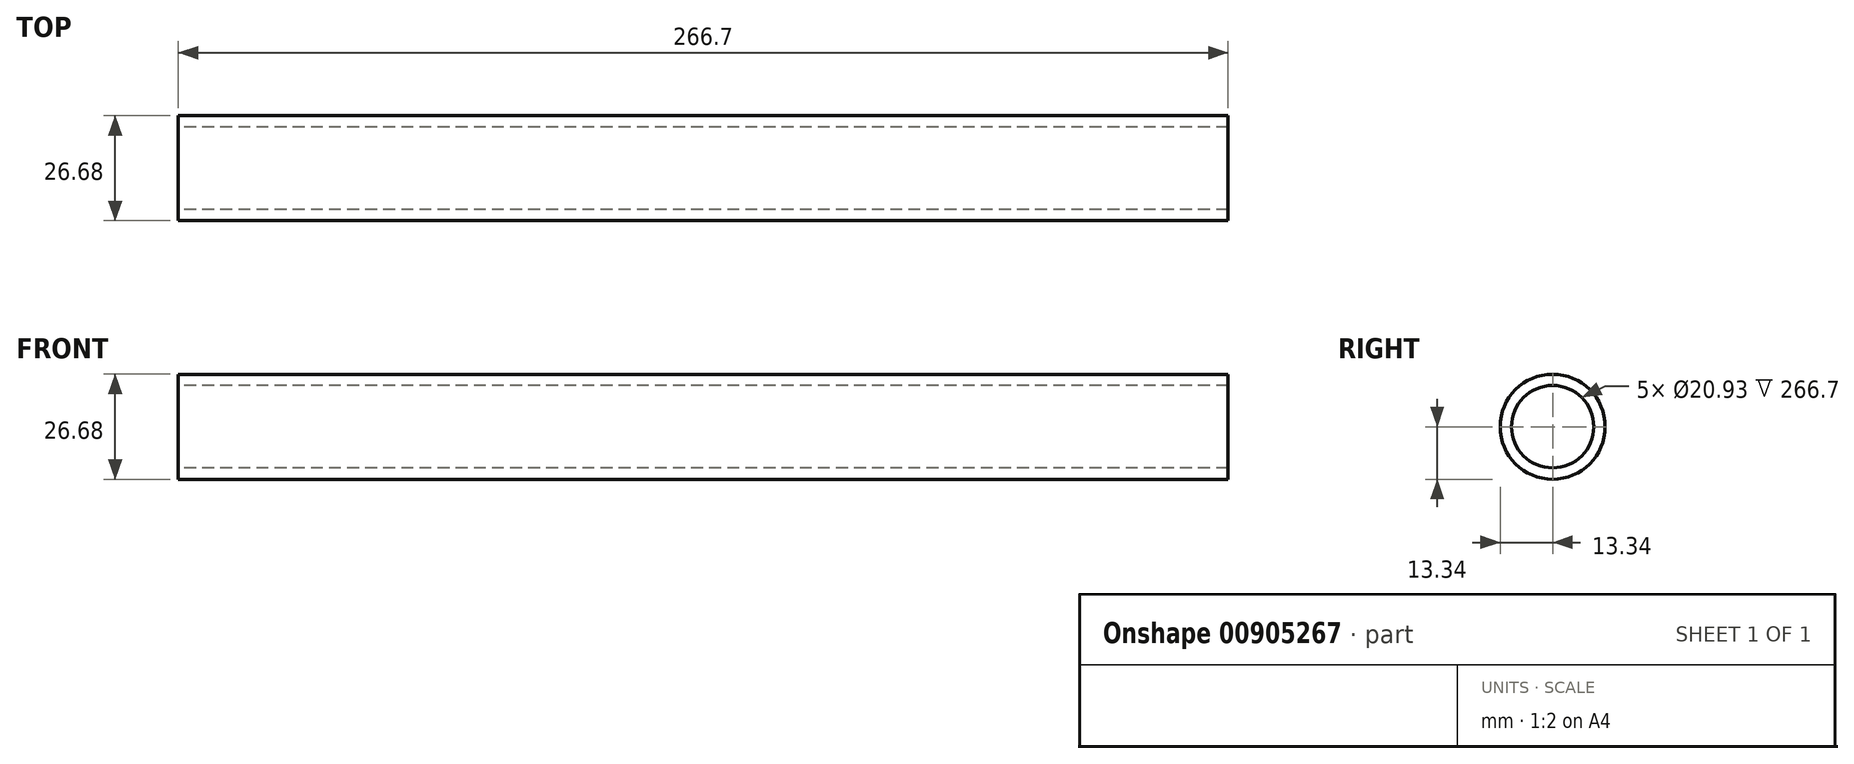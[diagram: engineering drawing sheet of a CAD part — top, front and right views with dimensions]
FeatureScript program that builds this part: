
annotation { "Feature Type Name" : "Feature", "Feature Type Description" : "" }
export const myFeature = defineFeature(function(context is Context, id is Id, definition is map)
    precondition{}
    {
        {
            var Q0;
            Q0=qCreatedBy(makeId("Right.planeOp"),FACE);
            var sketch = newSketch(context, id + "F0", { "sketchPlane" : qUnion([Q0])});
            skCircle(sketch, "E0", {"center": v(0, 0) * mm, "radius": 13.34 * mm});
            skCircle(sketch, "E1", {"center": v(0, 0) * mm, "radius": 10.46 * mm});
            skSolve(sketch);
        }
        {
            var Q0;
            Q0=qSketchRegion(id+"F0",true);
            extrude(context, id + "F1", {"entities" : qUnion([Q0]), "depth" : 266.7 * mm, "offsetDistance" : 25.4 * mm});
        }
    });
